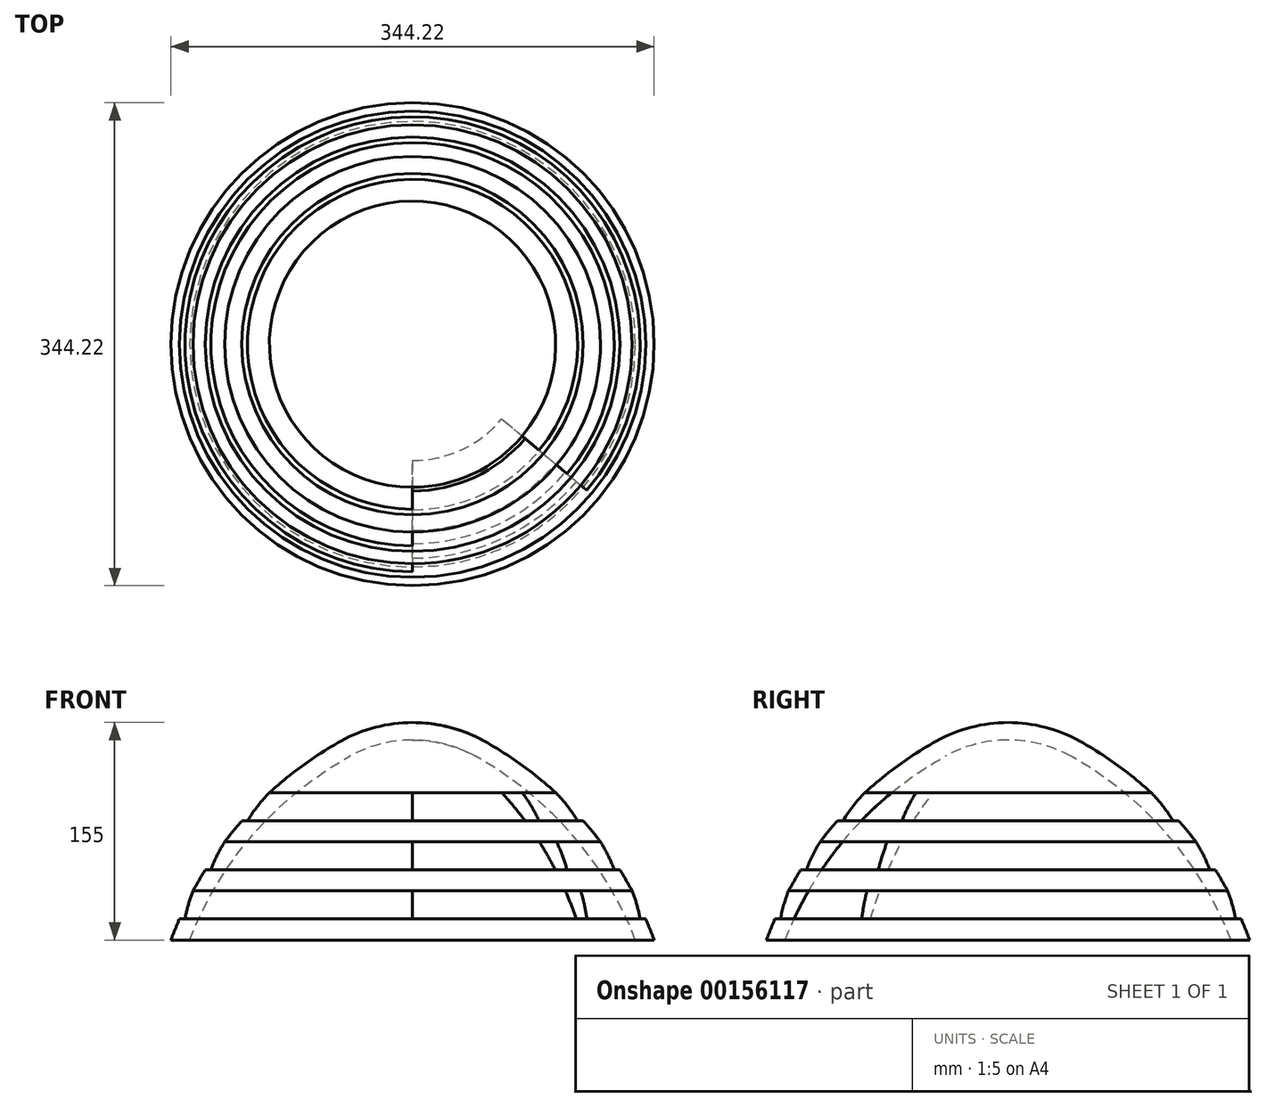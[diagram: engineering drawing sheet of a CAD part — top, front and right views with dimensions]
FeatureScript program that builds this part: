
annotation { "Feature Type Name" : "Feature", "Feature Type Description" : "" }
export const myFeature = defineFeature(function(context is Context, id is Id, definition is map)
    precondition{}
    {
        {
            var Q0;
            Q0=qCreatedBy(makeId("Front.planeOp"),FACE);
            var sketch = newSketch(context, id + "F0", { "sketchPlane" : qUnion([Q0])});
            skLineSegment(sketch, "E0", {"start": v(0, 0) * mm, "end": v(172.1, 0) * mm});
            skLineSegment(sketch, "E1", {"start": v(0, 0) * mm, "end": v(0, 155) * mm});
            skArc(sketch, "E2", {"start": v(172.1, 0) * mm, "mid": v(124.33, 81.8) * mm, "end": v(51, 141.78) * mm});
            skArc(sketch, "E3", {"start": v(51, 141.78) * mm, "mid": v(26.34, 151.64) * mm, "end": v(0, 155) * mm});
            skLineSegment(sketch, "E4", {"start": v(0, 155) * mm, "end": v(148.07, 155) * mm, "construction": true});
            skPoint(sketch, "E5.orphan", {"position": v(-172, 0) * mm});
            skSolve(sketch);
        }
        {
            var Q0;
            Q0=makeQuery(id+"F0.imprint","IMPRINT",FACE,{"disambiguationData":[TD([[makeQuery(id+"F0.imprint","IMPRINT",EDGE,{"derivedFrom":sQuery(id+"F0.wireOp",EDGE,"E0")}),1.0]])]});
            var Q1;
            Q1=sQuery(id+"F0.wireOp",EDGE,"E1");
            revolve(context, id + "F1", {"entities" : qUnion([Q0]), "axis" : qUnion([Q1]), "revolveType" : RevolveType.FULL});
        }
        {
            var Q0;
            Q0=qCreatedBy(makeId("Top.planeOp"),FACE);
            cPlane(context, id + "F2", {"entities" : qUnion([Q0]), "cplaneType" : CPlaneType.OFFSET, "offset" : 35 * mm, "width" : 150 * mm, "height" : 150 * mm});
        }
        {
            var Q0;
            Q0=makeQuery(id+"F1.opRevolve","SWEPT_FACE",FACE,{"disambiguationData":[OSD([sQuery(id+"F0.wireOp",EDGE,"E0")])]});
            shell(context, id + "F3", {"entities" : qUnion([Q0]), "thickness" : 12.5 * mm});
        }
        {
            var Q0;
            Q0=qCreatedBy(id+"F2.planeOp",FACE);
            var sketch = newSketch(context, id + "F4", { "sketchPlane" : qUnion([Q0])});
            skLineSegment(sketch, "E6", {"start": v(0, 0) * mm, "end": v(0, -185) * mm});
            skLineSegment(sketch, "E7", {"start": v(0, 0) * mm, "end": v(141.72, -118.92) * mm});
            skArc(sketch, "E8", {"start": v(0, -185) * mm, "mid": v(78.18, -167.67) * mm, "end": v(141.72, -118.92) * mm});
            skSolve(sketch);
        }
        {
            var Q0;
            Q0 = qSketchRegion(id + "F4", true);
            extrude(context, id + "F5", {"entities" : qUnion([Q0]), "operationType" : NewBodyOperationType.REMOVE, "oppositeDirection" : true, "depth" : 20 * mm});
        }
        {
            var Q0;
            Q0=qCreatedBy(id+"F2.planeOp",FACE);
            cPlane(context, id + "F6", {"entities" : qUnion([Q0]), "cplaneType" : CPlaneType.OFFSET, "offset" : 35 * mm, "width" : 150 * mm, "height" : 150 * mm});
        }
        {
            var Q0;
            Q0=qCreatedBy(id+"F6.planeOp",FACE);
            var sketch = newSketch(context, id + "F7", { "sketchPlane" : qUnion([Q0])});
            skLineSegment(sketch, "E9", {"start": v(0, 0) * mm, "end": v(0, -185) * mm});
            skLineSegment(sketch, "E10", {"start": v(0, 0) * mm, "end": v(141.72, -118.92) * mm});
            skArc(sketch, "E11", {"start": v(0, -185) * mm, "mid": v(78.18, -167.67) * mm, "end": v(141.72, -118.92) * mm});
            skSolve(sketch);
        }
        {
            var Q0;
            Q0 = qSketchRegion(id + "F7", true);
            extrude(context, id + "F8", {"entities" : qUnion([Q0]), "operationType" : NewBodyOperationType.REMOVE, "oppositeDirection" : true, "depth" : 20 * mm});
        }
        {
            var Q0;
            Q0=qCreatedBy(id+"F6.planeOp",FACE);
            cPlane(context, id + "F9", {"entities" : qUnion([Q0]), "cplaneType" : CPlaneType.OFFSET, "offset" : 35 * mm, "width" : 150 * mm, "height" : 150 * mm});
        }
        {
            var Q0;
            Q0=qCreatedBy(id+"F9.planeOp",FACE);
            var sketch = newSketch(context, id + "F10", { "sketchPlane" : qUnion([Q0])});
            skLineSegment(sketch, "E12", {"start": v(0, 0) * mm, "end": v(0, -185) * mm});
            skLineSegment(sketch, "E13", {"start": v(0, 0) * mm, "end": v(141.72, -118.92) * mm});
            skArc(sketch, "E14", {"start": v(0, -185) * mm, "mid": v(78.18, -167.67) * mm, "end": v(141.72, -118.92) * mm});
            skSolve(sketch);
        }
        {
            var Q0;
            Q0 = qSketchRegion(id + "F10", true);
            extrude(context, id + "F11", {"entities" : qUnion([Q0]), "operationType" : NewBodyOperationType.REMOVE, "oppositeDirection" : true, "depth" : 20 * mm});
        }
        {
            var Q0;
            Q0=qCreatedBy(makeId("Right.planeOp"),FACE);
            var sketch = newSketch(context, id + "F12", { "sketchPlane" : qUnion([Q0])});
            skArc(sketch, "E15.0", {"start": v(-51, 141.78) * mm, "mid": v(-77.57, 124.9) * mm, "end": v(-101.96, 105) * mm});
            skLineSegment(sketch, "E16", {"start": v(0, 0) * mm, "end": v(-172.1, 0) * mm, "construction": true});
            skPoint(sketch, "E17.orphan", {"position": v(-121.56, 85) * mm});
            skLineSegment(sketch, "E18", {"start": v(0, 0) * mm, "end": v(0, 155) * mm, "construction": true});
            skPoint(sketch, "E19.orphan", {"position": v(-101.96, 105) * mm});
            skArc(sketch, "E20", {"start": v(0, 155) * mm, "mid": v(-26.34, 151.64) * mm, "end": v(-51, 141.78) * mm});
            skArc(sketch, "E21", {"start": v(-101.96, 105) * mm, "mid": v(-110.37, 95.47) * mm, "end": v(-117.56, 85) * mm});
            skLineSegment(sketch, "E22", {"start": v(-121.56, 85) * mm, "end": v(-117.56, 85) * mm});
            skArc(sketch, "E23.trimOffspring", {"start": v(-121.56, 85) * mm, "mid": v(-127.84, 77.61) * mm, "end": v(-133.85, 70) * mm});
            skArc(sketch, "E24", {"start": v(-133.85, 70) * mm, "mid": v(-139.3, 60.26) * mm, "end": v(-143.67, 50) * mm});
            skLineSegment(sketch, "E25", {"start": v(-143.67, 50) * mm, "end": v(-147.67, 50) * mm});
            skArc(sketch, "E26.trimOffspring", {"start": v(-147.67, 50) * mm, "mid": v(-152.15, 42.57) * mm, "end": v(-156.39, 35) * mm});
            skArc(sketch, "E27", {"start": v(-156.39, 35) * mm, "mid": v(-159.74, 25.14) * mm, "end": v(-162.1, 15) * mm});
            skLineSegment(sketch, "E28", {"start": v(-162.1, 15) * mm, "end": v(-166.1, 15) * mm});
            skArc(sketch, "E29.trimOffspring", {"start": v(-166.1, 15) * mm, "mid": v(-169.22, 7.55) * mm, "end": v(-172.1, 0) * mm});
            skLineSegment(sketch, "E30", {"start": v(-172.1, 0) * mm, "end": v(-197.1, 0) * mm});
            skLineSegment(sketch, "E31", {"start": v(-197.1, 0) * mm, "end": v(-197.1, 185) * mm});
            skLineSegment(sketch, "E32", {"start": v(-197.1, 185) * mm, "end": v(0, 185) * mm});
            skLineSegment(sketch, "E33", {"start": v(0, 185) * mm, "end": v(0, 155) * mm});
            skSolve(sketch);
        }
        {
            var Q0;
            Q0 = qSketchRegion(id + "F12", true);
            var Q1;
            Q1=sQuery(id+"F12.wireOp",EDGE,"E18");
            revolve(context, id + "F13", {"operationType" : NewBodyOperationType.REMOVE, "entities" : qUnion([Q0]), "axis" : qUnion([Q1]), "revolveType" : RevolveType.FULL, "oppositeDirection" : true});
        }
    });
